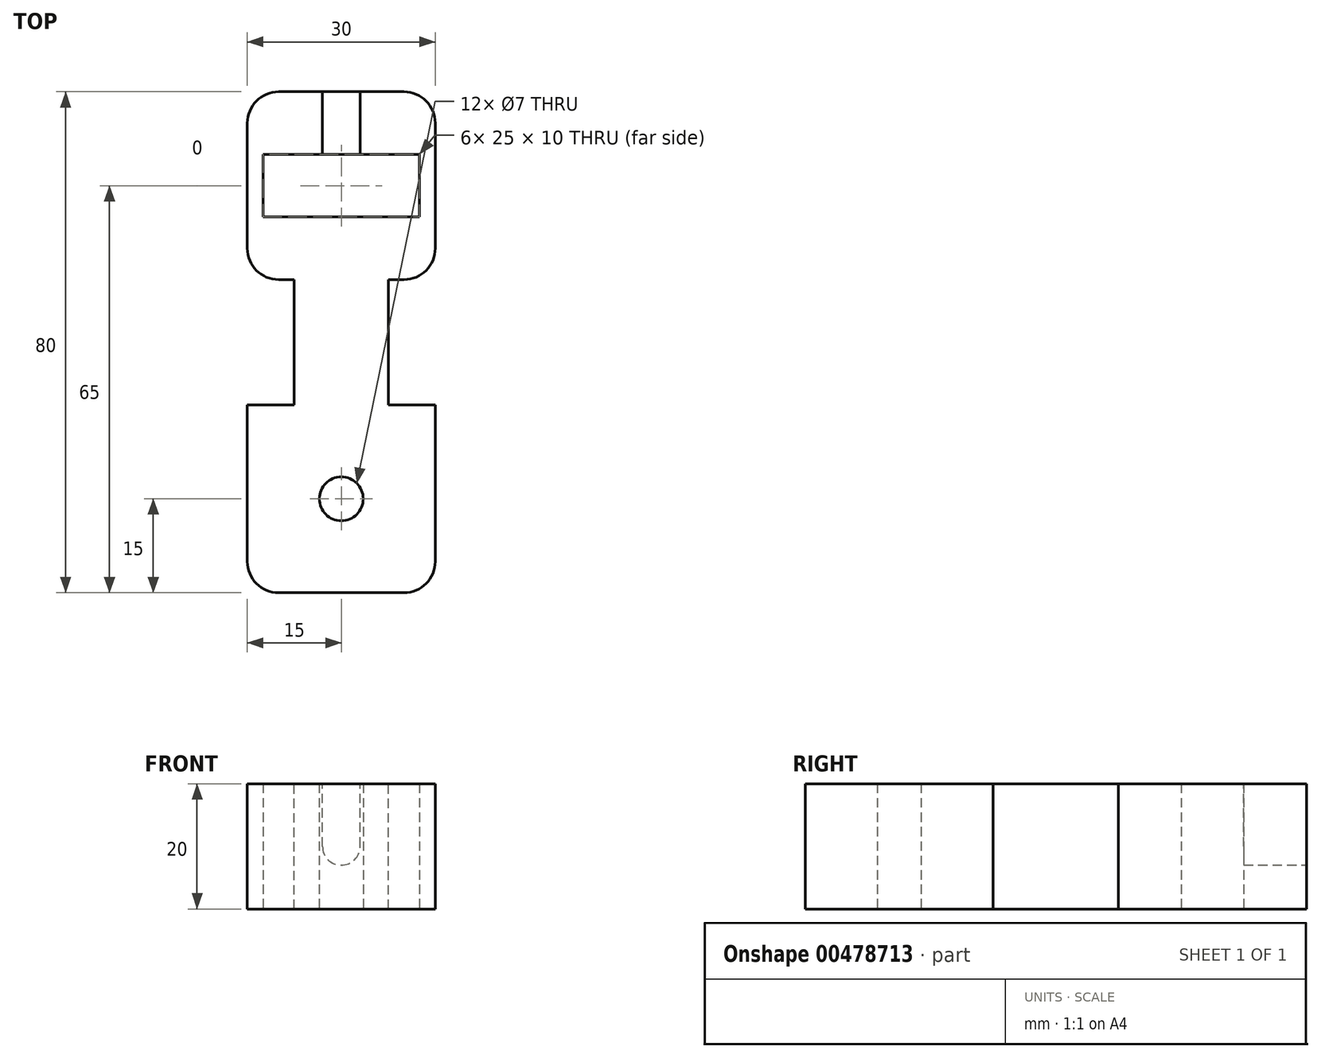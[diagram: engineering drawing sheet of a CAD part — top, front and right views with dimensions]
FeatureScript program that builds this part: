
annotation { "Feature Type Name" : "Feature", "Feature Type Description" : "" }
export const myFeature = defineFeature(function(context is Context, id is Id, definition is map)
    precondition{}
    {
        {
            var Q0;
            Q0=qCreatedBy(makeId("Top.planeOp"),FACE);
            var sketch = newSketch(context, id + "F0", { "sketchPlane" : qUnion([Q0])});
            skLineSegment(sketch, "E0.bottom", {"start": v(0, 0) * mm, "end": v(30, 0) * mm});
            skLineSegment(sketch, "E0.top", {"start": v(0, 80) * mm, "end": v(30, 80) * mm});
            skLineSegment(sketch, "E0.left", {"start": v(0, 0) * mm, "end": v(0, 80) * mm});
            skLineSegment(sketch, "E0.right", {"start": v(30, 0) * mm, "end": v(30, 80) * mm});
            skSolve(sketch);
        }
        {
            var Q0;
            Q0 = qSketchRegion(id + "F0", true);
            extrude(context, id + "F1", {"entities" : qUnion([Q0]), "depth" : 20 * mm});
        }
        {
            var Q0;
            Q0=qCreatedBy(makeId("Top.planeOp"),FACE);
            var sketch = newSketch(context, id + "F2", { "sketchPlane" : qUnion([Q0])});
            skCircle(sketch, "E1", {"center": v(15, 15) * mm, "radius": 3.5 * mm});
            skSolve(sketch);
        }
        {
            var Q0;
            Q0=makeQuery(id+"F2.imprint","IMPRINT",FACE,{"disambiguationData":[TD([[makeQuery(id+"F2.imprint","IMPRINT",EDGE,{"derivedFrom":sQuery(id+"F2.wireOp",EDGE,"E1")}),1.0]])]});
            var Q1;
            Q1=sQuery(id+"F2.wireOp",EDGE,"E1");
            extrude(context, id + "F3", {"entities" : qUnion([Q0]), "operationType" : NewBodyOperationType.REMOVE, "surfaceEntities" : qUnion([Q1]), "depth" : 20 * mm});
        }
        {
            var Q0;
            Q0=qCreatedBy(makeId("Top.planeOp"),FACE);
            var sketch = newSketch(context, id + "F4", { "sketchPlane" : qUnion([Q0])});
            skLineSegment(sketch, "E2.bottom", {"start": v(2.5, 70) * mm, "end": v(27.5, 70) * mm});
            skLineSegment(sketch, "E2.top", {"start": v(2.5, 60) * mm, "end": v(27.5, 60) * mm});
            skLineSegment(sketch, "E2.left", {"start": v(2.5, 70) * mm, "end": v(2.5, 60) * mm});
            skLineSegment(sketch, "E2.right", {"start": v(27.5, 70) * mm, "end": v(27.5, 60) * mm});
            skSolve(sketch);
        }
        {
            var Q0;
            Q0 = qSketchRegion(id + "F4", true);
            extrude(context, id + "F5", {"entities" : qUnion([Q0]), "operationType" : NewBodyOperationType.REMOVE, "depth" : 20 * mm});
        }
        {
            var Q0;
            Q0=makeQuery(id+"F1.opExtrude","SWEPT_FACE",FACE,{"disambiguationData":[OSD([sQuery(id+"F0.wireOp",EDGE,"E0.top")])]});
            var sketch = newSketch(context, id + "F6", { "sketchPlane" : qUnion([Q0])});
            skPoint(sketch, "E3.firstSnap0", {"position": v(-18, 0) * mm});
            skLineSegment(sketch, "E3.bottom", {"start": v(-18, 10) * mm, "end": v(-12, 10) * mm});
            skLineSegment(sketch, "E3.top", {"start": v(-18, 20) * mm, "end": v(-12, 20) * mm});
            skLineSegment(sketch, "E3.left", {"start": v(-18, 10) * mm, "end": v(-18, 20) * mm});
            skLineSegment(sketch, "E3.right", {"start": v(-12, 10) * mm, "end": v(-12, 20) * mm});
            skCircle(sketch, "E4", {"center": v(-15, 10) * mm, "radius": 3 * mm});
            skSolve(sketch);
        }
        {
            var Q0;
            Q0 = qSketchRegion(id + "F6", true);
            extrude(context, id + "F7", {"entities" : qUnion([Q0]), "operationType" : NewBodyOperationType.REMOVE, "oppositeDirection" : true, "depth" : 20 * mm});
        }
        {
            var Q0;
            Q0=makeQuery(id+"F1.opExtrude","CAP_FACE",FACE,{"disambiguationData":[OSD([sQuery(id+"F0.wireOp",EDGE,"E0.bottom"),sQuery(id+"F0.wireOp",EDGE,"E0.top"),sQuery(id+"F0.wireOp",EDGE,"E0.left"),sQuery(id+"F0.wireOp",EDGE,"E0.right")])],"isStart":false});
            var sketch = newSketch(context, id + "F8", { "sketchPlane" : qUnion([Q0])});
            skLineSegment(sketch, "E5.bottom", {"start": v(30, 50) * mm, "end": v(22.5, 50) * mm});
            skLineSegment(sketch, "E5.top", {"start": v(30, 30) * mm, "end": v(22.5, 30) * mm});
            skLineSegment(sketch, "E5.left", {"start": v(30, 50) * mm, "end": v(30, 30) * mm});
            skLineSegment(sketch, "E5.right", {"start": v(22.5, 50) * mm, "end": v(22.5, 30) * mm});
            skLineSegment(sketch, "E6.bottom", {"start": v(0, 50) * mm, "end": v(7.5, 50) * mm});
            skLineSegment(sketch, "E6.top", {"start": v(0, 30) * mm, "end": v(7.5, 30) * mm});
            skLineSegment(sketch, "E6.left", {"start": v(0, 50) * mm, "end": v(0, 30) * mm});
            skLineSegment(sketch, "E6.right", {"start": v(7.5, 50) * mm, "end": v(7.5, 30) * mm});
            skSolve(sketch);
        }
        {
            var Q0;
            Q0 = qSketchRegion(id + "F8", true);
            extrude(context, id + "F9", {"entities" : qUnion([Q0]), "operationType" : NewBodyOperationType.REMOVE, "oppositeDirection" : true, "depth" : 20 * mm});
        }
        {
            var Q0;
            Q0=makeQuery(id+"F9.boolean.opBoolean","COPY",EDGE,{"derivedFrom":makeQuery(id+"F9.opExtrude","SWEPT_EDGE",EDGE,{"disambiguationData":[OSD([sQuery(id+"F0.wireOp",EDGE,"E0.right"),sQuery(id+"F8.wireOp",EDGE,"E5.top"),sQuery(id+"F8.wireOp",EDGE,"E5.left")])]})});
            var Q1;
            Q1=makeQuery(id+"F9.boolean.opBoolean","COPY",EDGE,{"derivedFrom":makeQuery(id+"F9.opExtrude","SWEPT_EDGE",EDGE,{"disambiguationData":[OSD([sQuery(id+"F0.wireOp",EDGE,"E0.left"),sQuery(id+"F8.wireOp",EDGE,"E6.top"),sQuery(id+"F8.wireOp",EDGE,"E6.left")])]})});
            var Q2;
            Q2=makeQuery(id+"F1.opExtrude","SWEPT_EDGE",EDGE,{"disambiguationData":[OSD([sQuery(id+"F0.wireOp",EDGE,"E0.bottom"),sQuery(id+"F0.wireOp",EDGE,"E0.left")])]});
            var Q3;
            Q3=makeQuery(id+"F1.opExtrude","SWEPT_EDGE",EDGE,{"disambiguationData":[OSD([sQuery(id+"F0.wireOp",EDGE,"E0.bottom"),sQuery(id+"F0.wireOp",EDGE,"E0.right")])]});
            fillet(context, id + "F10", {"entities" : qUnion([Q0, Q1, Q2, Q3]), "radius" : 5 * mm, "tangentPropagation" : true, "allowEdgeOverflow" : false});
        }
        {
            var Q0;
            Q0=makeQuery(id+"F1.opExtrude","SWEPT_EDGE",EDGE,{"disambiguationData":[OSD([sQuery(id+"F0.wireOp",EDGE,"E0.top"),sQuery(id+"F0.wireOp",EDGE,"E0.left")])]});
            var Q1;
            Q1=makeQuery(id+"F9.boolean.opBoolean","COPY",EDGE,{"derivedFrom":makeQuery(id+"F9.opExtrude","SWEPT_EDGE",EDGE,{"disambiguationData":[OSD([sQuery(id+"F0.wireOp",EDGE,"E0.left"),sQuery(id+"F8.wireOp",EDGE,"E6.bottom"),sQuery(id+"F8.wireOp",EDGE,"E6.left")])]})});
            var Q2;
            Q2=makeQuery(id+"F9.boolean.opBoolean","COPY",EDGE,{"derivedFrom":makeQuery(id+"F9.opExtrude","SWEPT_EDGE",EDGE,{"disambiguationData":[OSD([sQuery(id+"F0.wireOp",EDGE,"E0.right"),sQuery(id+"F8.wireOp",EDGE,"E5.bottom"),sQuery(id+"F8.wireOp",EDGE,"E5.left")])]})});
            var Q3;
            Q3=makeQuery(id+"F1.opExtrude","SWEPT_EDGE",EDGE,{"disambiguationData":[OSD([sQuery(id+"F0.wireOp",EDGE,"E0.top"),sQuery(id+"F0.wireOp",EDGE,"E0.right")])]});
            fillet(context, id + "F11", {"entities" : qUnion([Q0, Q1, Q2, Q3]), "radius" : 5 * mm, "tangentPropagation" : true, "allowEdgeOverflow" : false});
        }
    });
